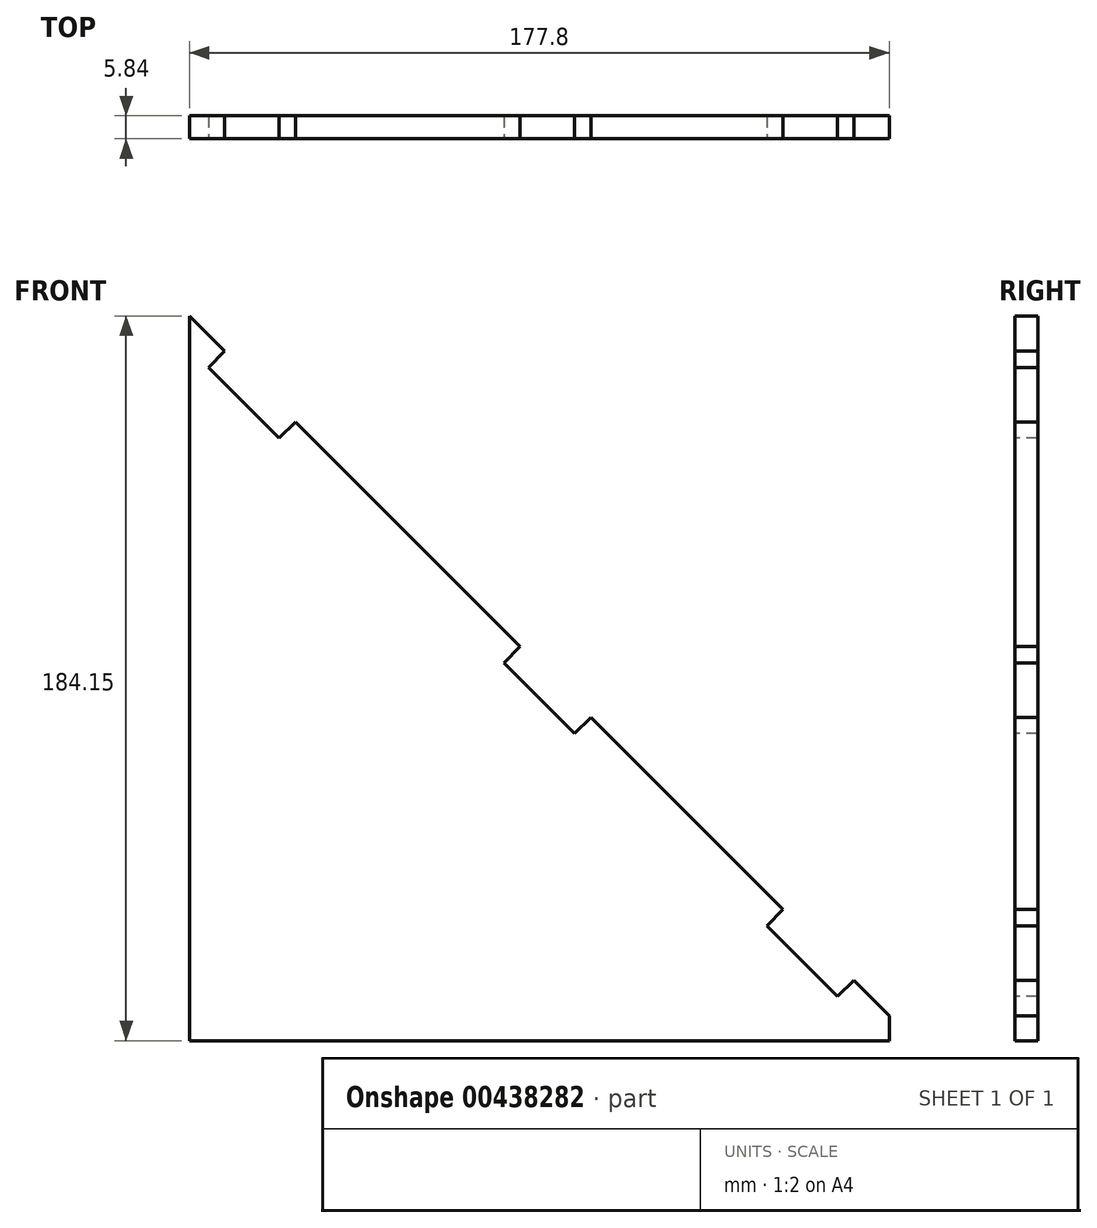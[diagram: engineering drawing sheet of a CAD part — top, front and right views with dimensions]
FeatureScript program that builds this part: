
annotation { "Feature Type Name" : "Feature", "Feature Type Description" : "" }
export const myFeature = defineFeature(function(context is Context, id is Id, definition is map)
    precondition{}
    {
        {
            var Q0;
            Q0=qCreatedBy(makeId("Front.planeOp"),FACE);
            var sketch = newSketch(context, id + "F0", { "sketchPlane" : qUnion([Q0])});
            skLineSegment(sketch, "E0", {"start": v(0, 184.15) * mm, "end": v(8.98, 175.17) * mm});
            skLineSegment(sketch, "E1", {"start": v(8.98, 175.17) * mm, "end": v(4.85, 171.04) * mm});
            skLineSegment(sketch, "E2", {"start": v(4.85, 171.04) * mm, "end": v(22.8, 153.08) * mm});
            skLineSegment(sketch, "E3", {"start": v(22.8, 153.08) * mm, "end": v(26.94, 157.2) * mm});
            skLineSegment(sketch, "E4", {"start": v(26.94, 157.2) * mm, "end": v(84.05, 100.1) * mm});
            skLineSegment(sketch, "E5", {"start": v(84.05, 100.1) * mm, "end": v(79.92, 95.97) * mm});
            skLineSegment(sketch, "E6", {"start": v(79.92, 95.97) * mm, "end": v(97.88, 78) * mm});
            skLineSegment(sketch, "E7", {"start": v(97.88, 78) * mm, "end": v(102.01, 82.14) * mm});
            skLineSegment(sketch, "E8", {"start": v(102.01, 82.14) * mm, "end": v(150.86, 33.3) * mm});
            skLineSegment(sketch, "E9", {"start": v(150.86, 33.3) * mm, "end": v(146.73, 29.16) * mm});
            skLineSegment(sketch, "E10", {"start": v(146.73, 29.16) * mm, "end": v(164.69, 11.2) * mm});
            skLineSegment(sketch, "E11", {"start": v(164.69, 11.2) * mm, "end": v(168.82, 15.33) * mm});
            skLineSegment(sketch, "E12", {"start": v(168.82, 15.33) * mm, "end": v(177.8, 6.35) * mm});
            skPoint(sketch, "E13", {"position": v(88.9, 86.99) * mm});
            skLineSegment(sketch, "E14", {"start": v(0, 184.15) * mm, "end": v(17.32, 201.47) * mm, "construction": true});
            skLineSegment(sketch, "E15", {"start": v(177.8, 6.35) * mm, "end": v(195.12, 23.67) * mm, "construction": true});
            skPoint(sketch, "E16", {"position": v(110.35, 108.43) * mm});
            skLineSegment(sketch, "E17", {"start": v(110.35, 108.43) * mm, "end": v(88.9, 86.99) * mm, "construction": true});
            skLineSegment(sketch, "E18", {"start": v(0, 184.15) * mm, "end": v(0, 0) * mm});
            skLineSegment(sketch, "E19", {"start": v(0, 0) * mm, "end": v(177.8, 0) * mm});
            skLineSegment(sketch, "E20", {"start": v(177.8, 0) * mm, "end": v(177.8, 6.35) * mm});
            skLineSegment(sketch, "E21.bottom", {"start": v(12.7, 0) * mm, "end": v(38.1, 0) * mm});
            skLineSegment(sketch, "E21.top", {"start": v(12.7, -5.84) * mm, "end": v(38.1, -5.84) * mm});
            skLineSegment(sketch, "E21.left", {"start": v(12.7, -5.84) * mm, "end": v(12.7, 0) * mm});
            skLineSegment(sketch, "E21.right", {"start": v(38.1, -5.84) * mm, "end": v(38.1, 0) * mm});
            skLineSegment(sketch, "E22.bottom", {"start": v(139.7, 0) * mm, "end": v(165.1, 0) * mm});
            skLineSegment(sketch, "E22.top", {"start": v(139.7, -5.84) * mm, "end": v(165.1, -5.84) * mm});
            skLineSegment(sketch, "E22.left", {"start": v(139.7, -5.84) * mm, "end": v(139.7, 0) * mm});
            skLineSegment(sketch, "E22.right", {"start": v(165.1, -5.84) * mm, "end": v(165.1, 0) * mm});
            skLineSegment(sketch, "E23.bottom", {"start": v(76.2, 0) * mm, "end": v(101.6, 0) * mm});
            skLineSegment(sketch, "E23.top", {"start": v(76.2, -5.84) * mm, "end": v(101.6, -5.84) * mm});
            skLineSegment(sketch, "E23.left", {"start": v(76.2, 0) * mm, "end": v(76.2, -5.84) * mm});
            skLineSegment(sketch, "E23.right", {"start": v(101.6, 0) * mm, "end": v(101.6, -5.84) * mm});
            skPoint(sketch, "E24", {"position": v(88.9, -5.84) * mm});
            skSolve(sketch);
        }
        {
            var Q0;
            Q0=makeQuery(id+"F0.imprint","IMPRINT",FACE,{"disambiguationData":[TD([[makeQuery(id+"F0.imprint","IMPRINT",EDGE,{"derivedFrom":sQuery(id+"F0.wireOp",EDGE,"E0")}),-1.0]])]});
            var Q1;
            Q1=makeQuery(id+"F0.imprint","IMPRINT",FACE,{"disambiguationData":[TD([[makeQuery(id+"F0.imprint","IMPRINT",EDGE,{"derivedFrom":sQuery(id+"F0.wireOp",EDGE,"E21.bottom")}),-1.0]])]});
            var Q2;
            Q2=makeQuery(id+"F0.imprint","IMPRINT",FACE,{"disambiguationData":[TD([[makeQuery(id+"F0.imprint","IMPRINT",EDGE,{"derivedFrom":sQuery(id+"F0.wireOp",EDGE,"E22.bottom")}),-1.0]])]});
            var Q3;
            Q3=makeQuery(id+"F0.imprint","IMPRINT",FACE,{"disambiguationData":[TD([[makeQuery(id+"F0.imprint","IMPRINT",EDGE,{"derivedFrom":sQuery(id+"F0.wireOp",EDGE,"E23.bottom")}),-1.0]])]});
            extrude(context, id + "F1", {"entities" : qUnion([Q0, Q1, Q2, Q3]), "oppositeDirection" : true, "depth" : 5.84 * mm});
        }
    });
